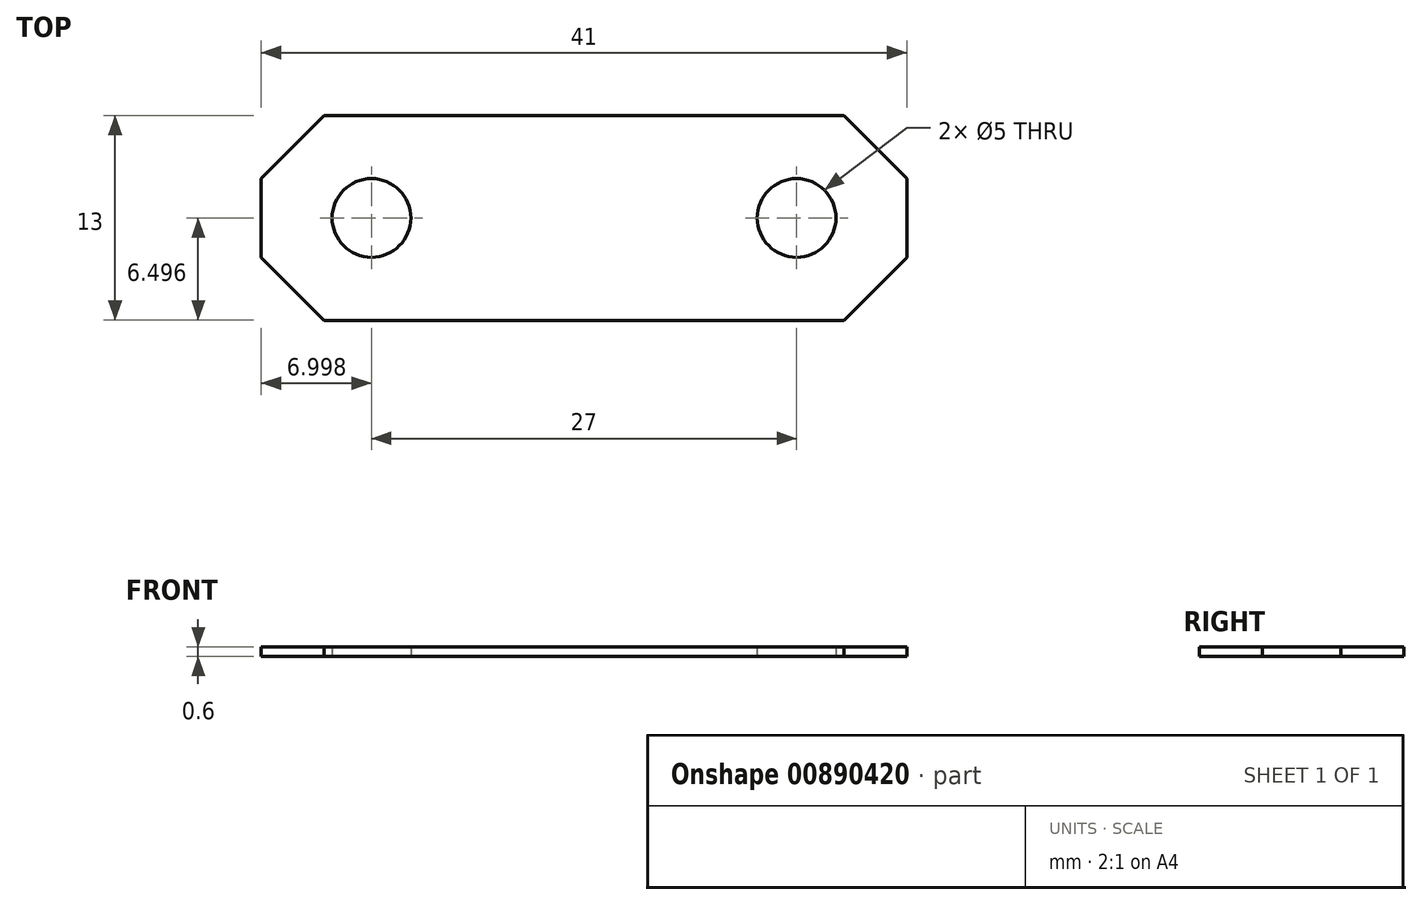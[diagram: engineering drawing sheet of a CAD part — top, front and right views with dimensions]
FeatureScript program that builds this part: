
annotation { "Feature Type Name" : "Feature", "Feature Type Description" : "" }
export const myFeature = defineFeature(function(context is Context, id is Id, definition is map)
    precondition{}
    {
        {
            var Q0;
            Q0=qCreatedBy(makeId("Top.planeOp"),FACE);
            var sketch = newSketch(context, id + "F0", { "sketchPlane" : qUnion([Q0])});
            skLineSegment(sketch, "E0", {"start": v(-45, 13.03) * mm, "end": v(-49, 9.03) * mm});
            skLineSegment(sketch, "E1", {"start": v(-28.5, 16.31) * mm, "end": v(-28.5, -10.51) * mm, "construction": true});
            skLineSegment(sketch, "E2.MirrorCS", {"start": v(-12, 13.03) * mm, "end": v(-8, 9.03) * mm});
            skLineSegment(sketch, "E3", {"start": v(-52.94, 6.53) * mm, "end": v(-5.55, 6.53) * mm, "construction": true});
            skLineSegment(sketch, "E4.MirrorCS", {"start": v(-45, 0.03) * mm, "end": v(-49, 4.03) * mm});
            skLineSegment(sketch, "E5.MirrorCS", {"start": v(-12, 0.03) * mm, "end": v(-8, 4.03) * mm});
            skLineSegment(sketch, "E6", {"start": v(-49, 4.03) * mm, "end": v(-49, 9.03) * mm});
            skLineSegment(sketch, "E7", {"start": v(-45, 13.03) * mm, "end": v(-12, 13.03) * mm});
            skLineSegment(sketch, "E8", {"start": v(-8, 9.03) * mm, "end": v(-8, 4.03) * mm});
            skLineSegment(sketch, "E9", {"start": v(-12, 0.03) * mm, "end": v(-45, 0.03) * mm});
            skCircle(sketch, "E10", {"center": v(-15, 6.53) * mm, "radius": 2.5 * mm});
            skCircle(sketch, "E11.MirrorC", {"center": v(-42, 6.53) * mm, "radius": 2.5 * mm});
            skSolve(sketch);
        }
        {
            var Q0;
            Q0=makeQuery(id+"F0.imprint","IMPRINT",FACE,{"disambiguationData":[TD([[makeQuery(id+"F0.imprint","IMPRINT",EDGE,{"derivedFrom":sQuery(id+"F0.wireOp",EDGE,"E0")}),1.0]])]});
            extrude(context, id + "F1", {"entities" : qUnion([Q0]), "depth" : 0.6 * mm, "offsetDistance" : 25 * mm});
        }
    });
